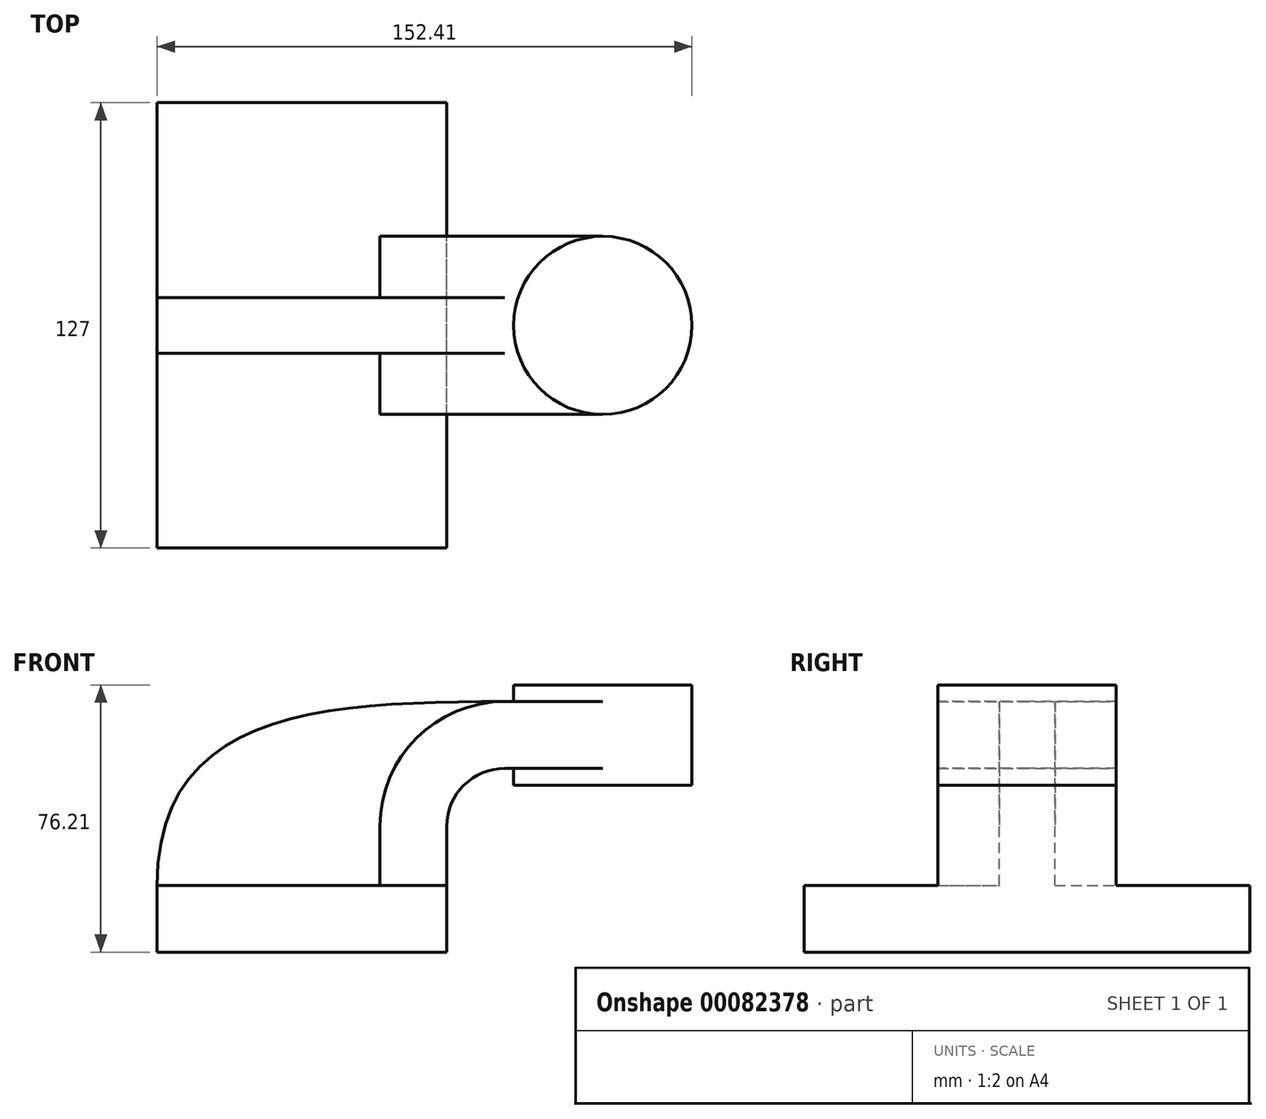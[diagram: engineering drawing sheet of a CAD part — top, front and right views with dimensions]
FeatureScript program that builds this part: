
annotation { "Feature Type Name" : "Feature", "Feature Type Description" : "" }
export const myFeature = defineFeature(function(context is Context, id is Id, definition is map)
    precondition{}
    {
        {
            var Q0;
            Q0=qCreatedBy(makeId("Front.planeOp"),FACE);
            var sketch = newSketch(context, id + "F0", { "sketchPlane" : qUnion([Q0])});
            skLineSegment(sketch, "E0.bottom", {"start": v(41.28, -9.52) * mm, "end": v(-41.28, -9.53) * mm});
            skLineSegment(sketch, "E0.top", {"start": v(41.27, 9.53) * mm, "end": v(-41.28, 9.53) * mm});
            skLineSegment(sketch, "E0.left", {"start": v(41.28, -9.52) * mm, "end": v(41.28, 9.53) * mm});
            skLineSegment(sketch, "E0.right", {"start": v(-41.28, -9.53) * mm, "end": v(-41.28, 9.53) * mm});
            skPoint(sketch, "E0.middle", {"position": v(0, 0) * mm});
            skLineSegment(sketch, "E1.bottom", {"start": v(111.12, 38.1) * mm, "end": v(60.32, 38.1) * mm});
            skLineSegment(sketch, "E1.top", {"start": v(111.12, 66.68) * mm, "end": v(60.32, 66.68) * mm});
            skLineSegment(sketch, "E1.left", {"start": v(111.13, 38.1) * mm, "end": v(111.12, 66.68) * mm});
            skLineSegment(sketch, "E1.right", {"start": v(60.32, 38.1) * mm, "end": v(60.32, 66.68) * mm});
            skPoint(sketch, "E1.middle", {"position": v(85.72, 52.39) * mm});
            skLineSegment(sketch, "E2", {"start": v(41.27, 9.53) * mm, "end": v(41.27, 26.37) * mm});
            skArc(sketch, "E3", {"start": v(41.27, 26.37) * mm, "mid": v(46.11, 38.04) * mm, "end": v(57.79, 42.88) * mm});
            skLineSegment(sketch, "E4", {"start": v(57.79, 42.88) * mm, "end": v(85.72, 42.88) * mm});
            skLineSegment(sketch, "E5.0", {"start": v(57.79, 61.93) * mm, "end": v(85.72, 61.93) * mm});
            skArc(sketch, "E5.1", {"start": v(22.22, 26.37) * mm, "mid": v(32.64, 51.5) * mm, "end": v(57.79, 61.93) * mm});
            skLineSegment(sketch, "E5.2", {"start": v(22.22, 9.53) * mm, "end": v(22.22, 26.37) * mm});
            skLineSegment(sketch, "E6", {"start": v(85.72, 38.1) * mm, "end": v(85.72, 66.68) * mm});
            skFitSpline(sketch, "E7", {"points": [v(-41.28, 9.53) * mm, v(57.79, 61.93) * mm], "startDerivative": vector(-0.2, 150.97) * mm, "endDerivative": vector(152.23, 0.13) * mm});
            skSolve(sketch);
        }
        {
            var Q0;
            Q0=makeQuery(id+"F0.imprint","IMPRINT",FACE,{"disambiguationData":[TD([[makeQuery(id+"F0.imprint","IMPRINT",EDGE,{"derivedFrom":sQuery(id+"F0.wireOp",EDGE,"E0.bottom")}),-1.0]])]});
            extrude(context, id + "F1", {"entities" : qUnion([Q0]), "endBound" : BoundingType.SYMMETRIC, "depth" : 127 * mm});
        }
        {
            var Q0;
            {var subQ1=sQuery(id+"F0.wireOp",EDGE,"E2");Q0=makeQuery(id+"F0.imprint","IMPRINT",FACE,{"disambiguationData":[TD([[makeQuery(id+"F0.imprint","IMPRINT",EDGE,{"derivedFrom":subQ1}),1.0]])]});}
            var Q1;
            {var subQ0=sQuery(id+"F0.wireOp",EDGE,"E4");var subQ1=sQuery(id+"F0.wireOp",EDGE,"E1.right");var subQ2=makeQuery(id+"F0.imprint","INTERSECT",VERTEX,{"derivedFrom":[subQ1,subQ0]});Q1=makeQuery(id+"F0.imprint","IMPRINT",FACE,{"disambiguationData":[TD([[makeQuery(id+"F0.imprint","IMPRINT",EDGE,{"disambiguationData":[TD([[subQ2,-1.0]])],"derivedFrom":subQ1}),-1.0]])]});}
            extrude(context, id + "F2", {"entities" : qUnion([Q0, Q1]), "operationType" : NewBodyOperationType.ADD, "endBound" : BoundingType.SYMMETRIC, "depth" : 50.8 * mm});
        }
        {
            var Q0;
            {var subQ3=sQuery(id+"F0.wireOp",EDGE,"E5.2");Q0=makeQuery(id+"F0.imprint","IMPRINT",FACE,{"disambiguationData":[TD([[makeQuery(id+"F0.imprint","IMPRINT",EDGE,{"derivedFrom":subQ3}),1.0]])]});}
            extrude(context, id + "F3", {"entities" : qUnion([Q0]), "operationType" : NewBodyOperationType.ADD, "endBound" : BoundingType.SYMMETRIC, "depth" : 15.88 * mm});
        }
        {
            var Q0;
            {var subQ0=sQuery(id+"F0.wireOp",EDGE,"E1.left");Q0=makeQuery(id+"F0.imprint","IMPRINT",FACE,{"disambiguationData":[TD([[makeQuery(id+"F0.imprint","IMPRINT",EDGE,{"derivedFrom":subQ0}),1.0]])]});}
            var Q1;
            Q1=sQuery(id+"F0.wireOp",EDGE,"E6");
            revolve(context, id + "F4", {"operationType" : NewBodyOperationType.ADD, "entities" : qUnion([Q0]), "axis" : qUnion([Q1]), "revolveType" : RevolveType.FULL});
        }
    });
